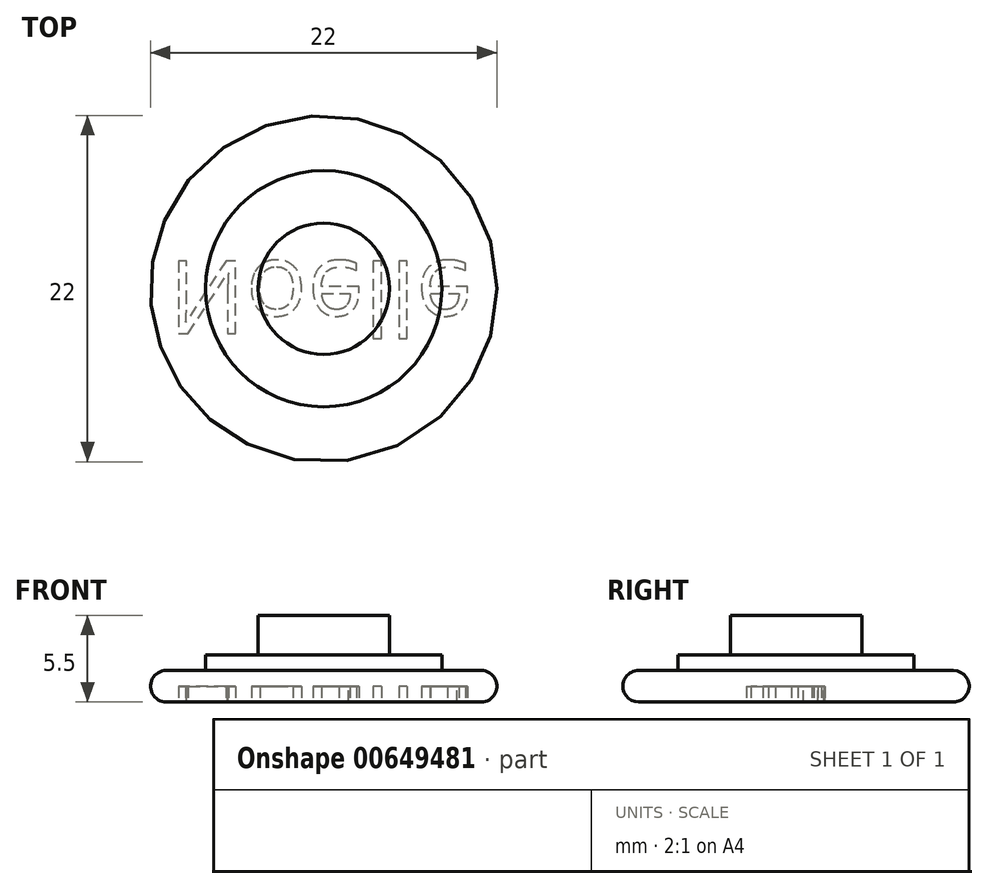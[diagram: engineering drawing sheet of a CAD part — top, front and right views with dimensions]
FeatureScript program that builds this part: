
annotation { "Feature Type Name" : "Feature", "Feature Type Description" : "" }
export const myFeature = defineFeature(function(context is Context, id is Id, definition is map)
    precondition{}
    {
        {
            var Q0;
            Q0=qCreatedBy(makeId("Top.planeOp"),FACE);
            var sketch = newSketch(context, id + "F0", { "sketchPlane" : qUnion([Q0])});
            skCircle(sketch, "E0", {"center": v(0, 0) * mm, "radius": 11 * mm});
            skCircle(sketch, "E1", {"center": v(0, 0) * mm, "radius": 7.5 * mm});
            skCircle(sketch, "E2", {"center": v(0, 0) * mm, "radius": 4.17 * mm});
            skSolve(sketch);
        }
        {
            var Q0;
            Q0=makeQuery(id+"F0.imprint","IMPRINT",FACE,{"disambiguationData":[TD([[makeQuery(id+"F0.imprint","IMPRINT",EDGE,{"derivedFrom":sQuery(id+"F0.wireOp",EDGE,"E0")}),1.0]])]});
            extrude(context, id + "F1", {"entities" : qUnion([Q0]), "depth" : 2 * mm, "offsetDistance" : 25 * mm});
        }
        {
            var Q0;
            Q0=makeQuery(id+"F0.imprint","IMPRINT",FACE,{"disambiguationData":[TD([[makeQuery(id+"F0.imprint","IMPRINT",EDGE,{"derivedFrom":sQuery(id+"F0.wireOp",EDGE,"E1")}),1.0]])]});
            extrude(context, id + "F2", {"entities" : qUnion([Q0]), "operationType" : NewBodyOperationType.ADD, "depth" : 3 * mm, "offsetDistance" : 25 * mm});
        }
        {
            var Q0;
            Q0=makeQuery(id+"F0.imprint","IMPRINT",FACE,{"disambiguationData":[TD([[makeQuery(id+"F0.imprint","IMPRINT",EDGE,{"derivedFrom":sQuery(id+"F0.wireOp",EDGE,"E2")}),1.0]])]});
            extrude(context, id + "F3", {"entities" : qUnion([Q0]), "operationType" : NewBodyOperationType.ADD, "depth" : 5.5 * mm, "offsetDistance" : 25 * mm});
        }
        {
            var Q0;
            Q0=makeQuery(id+"F1.opExtrude","CAP_EDGE",EDGE,{"disambiguationData":[OSD([sQuery(id+"F0.wireOp",EDGE,"E0")])],"isStart":false});
            var Q1;
            Q1=makeQuery(id+"F1.opExtrude","CAP_EDGE",EDGE,{"disambiguationData":[OSD([sQuery(id+"F0.wireOp",EDGE,"E0")])],"isStart":true});
            fillet(context, id + "F4", {"entities" : qUnion([Q0, Q1]), "radius" : 1 * mm, "tangentPropagation" : true, "allowEdgeOverflow" : false});
        }
        {
            var Q0;
            {var subQ0=sQuery(id+"F0.wireOp",EDGE,"E2");var subQ1=sQuery(id+"F0.wireOp",EDGE,"E1");Q0=makeQuery(id+"F3.boolean.opBoolean","MERGE",FACE,{"derivedFrom":[makeQuery(id+"F2.boolean.opBoolean","MERGE",FACE,{"derivedFrom":[makeQuery(id+"F1.opExtrude","CAP_FACE",FACE,{"disambiguationData":[OSD([sQuery(id+"F0.wireOp",EDGE,"E0"),subQ1])],"isStart":true}),makeQuery(id+"F2.opExtrude","CAP_FACE",FACE,{"disambiguationData":[OSD([subQ1,subQ0])],"isStart":true})]}),makeQuery(id+"F3.opExtrude","CAP_FACE",FACE,{"disambiguationData":[OSD([subQ0])],"isStart":true})]});}
            var sketch = newSketch(context, id + "F5", { "sketchPlane" : qUnion([Q0])});
            skText(sketch, "E3", { "text": "Noelle", "fontName": "OpenSans-Regular.ttf"});
            const initialGuessF5  = {"E3": [-0.00984, -0.00177, 1, 0, 0.00466]};
            skSetInitialGuess(sketch, initialGuessF5);
            skSolve(sketch);
        }
        {
            var Q0;
            Q0 = qSketchRegion(id + "F5", true);
            extrude(context, id + "F6", {"entities" : qUnion([Q0]), "operationType" : NewBodyOperationType.REMOVE, "oppositeDirection" : true, "depth" : 1 * mm, "offsetDistance" : 25 * mm});
        }
    });
